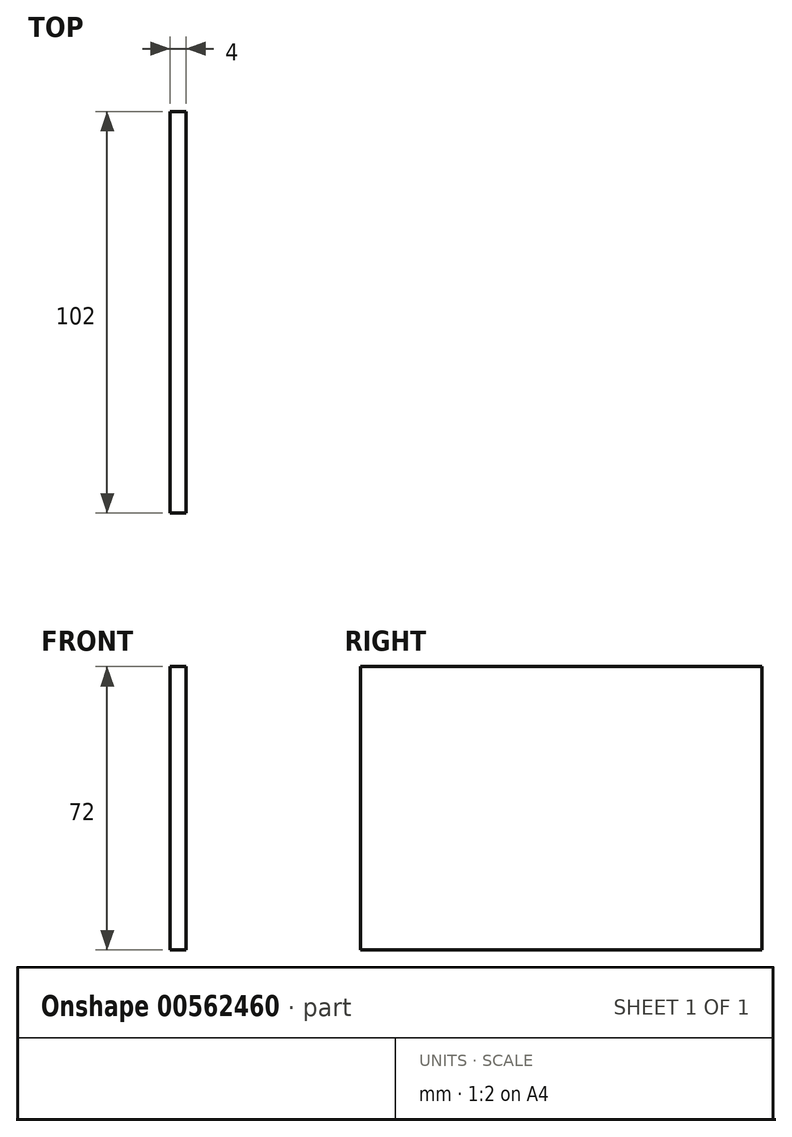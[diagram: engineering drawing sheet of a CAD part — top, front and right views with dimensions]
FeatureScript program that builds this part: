
annotation { "Feature Type Name" : "Feature", "Feature Type Description" : "" }
export const myFeature = defineFeature(function(context is Context, id is Id, definition is map)
    precondition{}
    {
        {
            var Q0;
            Q0=qCreatedBy(makeId("Right.planeOp"),FACE);
            var sketch = newSketch(context, id + "F0", { "sketchPlane" : qUnion([Q0])});
            skLineSegment(sketch, "E0.bottom", {"start": v(-51, 36) * mm, "end": v(51, 36) * mm});
            skLineSegment(sketch, "E0.top", {"start": v(-51, -36) * mm, "end": v(51, -36) * mm});
            skLineSegment(sketch, "E0.left", {"start": v(-51, 36) * mm, "end": v(-51, -36) * mm});
            skLineSegment(sketch, "E0.right", {"start": v(51, 36) * mm, "end": v(51, -36) * mm});
            skPoint(sketch, "E0.middle", {"position": v(0, 0) * mm});
            skSolve(sketch);
        }
        {
            var Q0;
            Q0=makeQuery(id+"F0.imprint","IMPRINT",FACE,{"disambiguationData":[TD([[makeQuery(id+"F0.imprint","IMPRINT",EDGE,{"derivedFrom":sQuery(id+"F0.wireOp",EDGE,"E0.bottom")}),-1.0]])]});
            extrude(context, id + "F1", {"entities" : qUnion([Q0]), "depth" : 4 * mm, "offsetDistance" : 25 * mm, "symmetric" : true});
        }
    });
